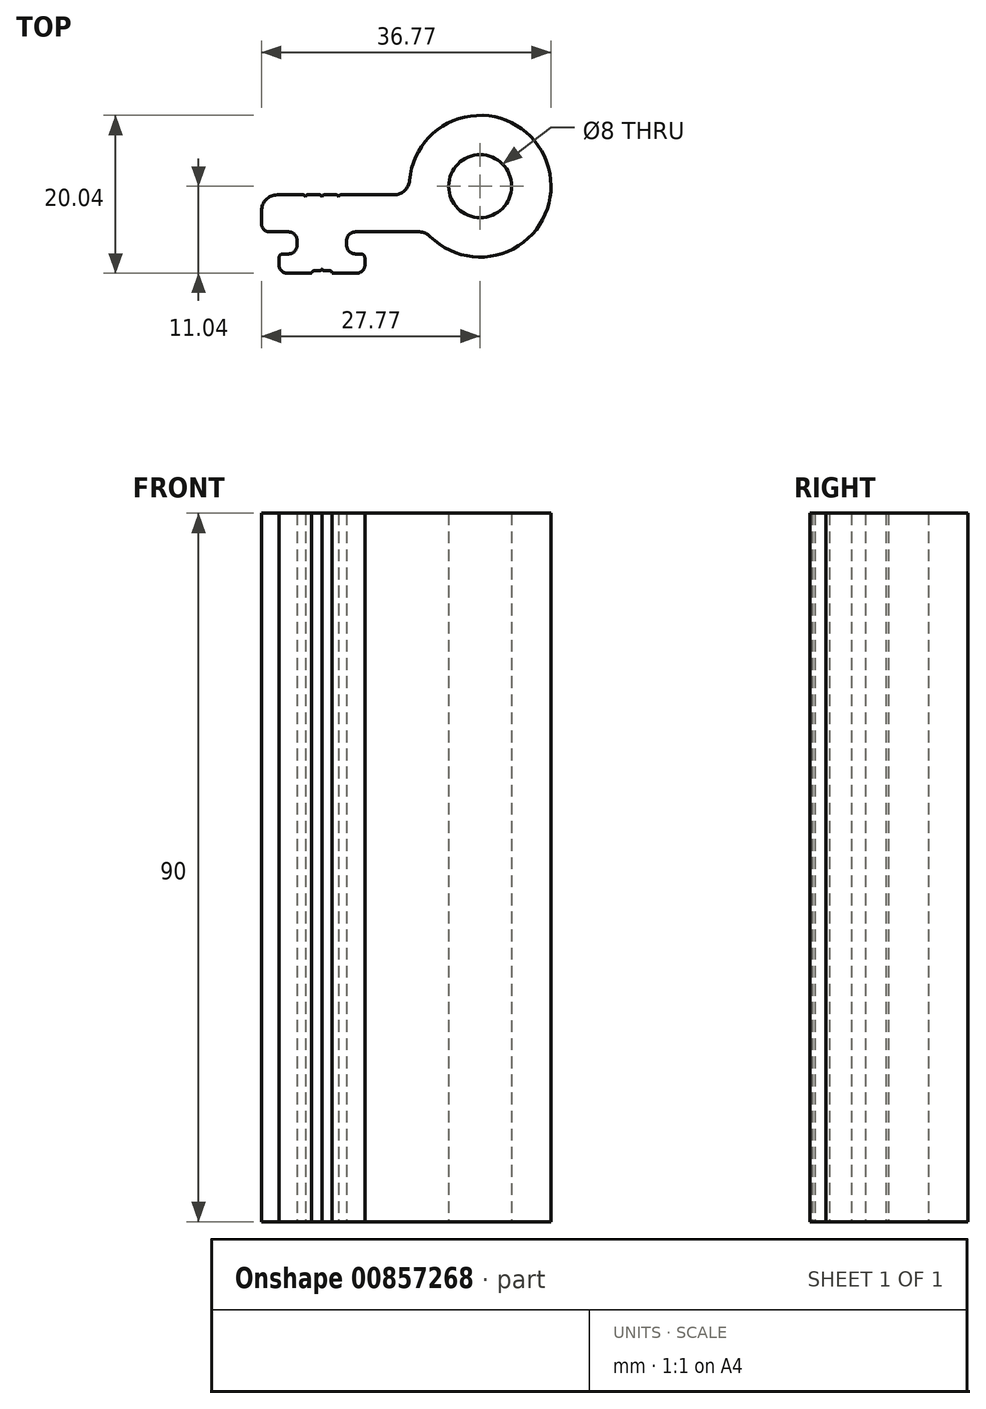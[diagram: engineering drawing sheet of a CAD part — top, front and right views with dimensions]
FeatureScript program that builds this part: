
annotation { "Feature Type Name" : "Feature", "Feature Type Description" : "" }
export const myFeature = defineFeature(function(context is Context, id is Id, definition is map)
    precondition{}
    {
        {
            var Q0;
            Q0=qCreatedBy(makeId("Top.planeOp"),FACE);
            var sketch = newSketch(context, id + "F0", { "sketchPlane" : qUnion([Q0])});
            skCircle(sketch, "E0", {"center": v(0, 0) * mm, "radius": 9 * mm});
            skCircle(sketch, "E1", {"center": v(0, 0) * mm, "radius": 4 * mm});
            skLineSegment(sketch, "E2", {"start": v(0, 0) * mm, "end": v(-45.8, 0) * mm, "construction": true});
            skLineSegment(sketch, "E3", {"start": v(-22.5, -1.1) * mm, "end": v(-25.77, -1.1) * mm});
            skLineSegment(sketch, "E4", {"start": v(-27.77, -3.1) * mm, "end": v(-27.77, -4.8) * mm});
            skLineSegment(sketch, "E5", {"start": v(-26.77, -5.8) * mm, "end": v(-24.35, -5.8) * mm});
            skPoint(sketch, "E6.visualSharp", {"position": v(-27.77, -1.1) * mm});
            skArc(sketch, "E6.filletArc", {"start": v(-25.77, -1.1) * mm, "mid": v(-27.18, -1.69) * mm, "end": v(-27.77, -3.1) * mm});
            skLineSegment(sketch, "E7", {"start": v(-23.25, -6.9) * mm, "end": v(-23.25, -7.5) * mm});
            skLineSegment(sketch, "E8", {"start": v(-24.35, -8.6) * mm, "end": v(-25.05, -8.6) * mm});
            skLineSegment(sketch, "E9", {"start": v(-25.55, -9.1) * mm, "end": v(-25.55, -10.04) * mm});
            skLineSegment(sketch, "E10", {"start": v(-24.55, -11.04) * mm, "end": v(-21.4, -11.04) * mm});
            skLineSegment(sketch, "E11", {"start": v(-14.65, -10.04) * mm, "end": v(-14.65, -9.1) * mm});
            skLineSegment(sketch, "E12", {"start": v(-15.15, -8.6) * mm, "end": v(-15.85, -8.6) * mm});
            skLineSegment(sketch, "E13", {"start": v(-16.95, -7.5) * mm, "end": v(-16.95, -6.9) * mm});
            skArc(sketch, "E14.filletArc", {"start": v(-15.65, -11.04) * mm, "mid": v(-14.94, -10.75) * mm, "end": v(-14.65, -10.04) * mm});
            skArc(sketch, "E15.filletArc", {"start": v(-25.55, -10.04) * mm, "mid": v(-25.26, -10.75) * mm, "end": v(-24.55, -11.04) * mm});
            skArc(sketch, "E16.filletArc", {"start": v(-22.2, -1.4) * mm, "mid": v(-22.29, -1.19) * mm, "end": v(-22.5, -1.1) * mm});
            skLineSegment(sketch, "E17", {"start": v(-21.72, -1.1) * mm, "end": v(-20.4, -1.1) * mm});
            skLineSegment(sketch, "E18", {"start": v(-17.7, -1.1) * mm, "end": v(-8.93, -1.1) * mm});
            skArc(sketch, "E19.filletArc", {"start": v(-18, -1.4) * mm, "mid": v(-18.09, -1.19) * mm, "end": v(-18.3, -1.1) * mm});
            skArc(sketch, "E20.filletArc", {"start": v(-17.7, -1.1) * mm, "mid": v(-17.91, -1.19) * mm, "end": v(-18, -1.4) * mm});
            skLineSegment(sketch, "E21", {"start": v(-19.8, -1.1) * mm, "end": v(-18.3, -1.1) * mm});
            skLineSegment(sketch, "E22", {"start": v(-21.4, -11.01) * mm, "end": v(-21.4, -11.04) * mm});
            skLineSegment(sketch, "E23", {"start": v(-19.8, -10.74) * mm, "end": v(-19.1, -10.74) * mm});
            skLineSegment(sketch, "E24", {"start": v(-18.8, -11.04) * mm, "end": v(-18.8, -11.04) * mm});
            skArc(sketch, "E25.filletArc", {"start": v(-21.1, -10.74) * mm, "mid": v(-21.31, -10.83) * mm, "end": v(-21.4, -11.04) * mm});
            skArc(sketch, "E26.filletArc", {"start": v(-18.8, -11.04) * mm, "mid": v(-18.89, -10.83) * mm, "end": v(-19.1, -10.74) * mm});
            skArc(sketch, "E27.filletArc", {"start": v(-20.1, -1.4) * mm, "mid": v(-20.19, -1.19) * mm, "end": v(-20.4, -1.1) * mm});
            skLineSegment(sketch, "E28.trimOffspring", {"start": v(-18.8, -11.04) * mm, "end": v(-15.65, -11.04) * mm});
            skArc(sketch, "E29.filletArc", {"start": v(-27.77, -4.8) * mm, "mid": v(-27.48, -5.5) * mm, "end": v(-26.77, -5.8) * mm});
            skArc(sketch, "E30.filletArc", {"start": v(-23.25, -6.9) * mm, "mid": v(-23.57, -6.12) * mm, "end": v(-24.35, -5.8) * mm});
            skArc(sketch, "E31.filletArc", {"start": v(-24.35, -8.6) * mm, "mid": v(-23.57, -8.28) * mm, "end": v(-23.25, -7.5) * mm});
            skArc(sketch, "E32.filletArc", {"start": v(-25.05, -8.6) * mm, "mid": v(-25.4, -8.75) * mm, "end": v(-25.55, -9.1) * mm});
            skLineSegment(sketch, "E33", {"start": v(-15.85, -5.8) * mm, "end": v(-6.88, -5.8) * mm});
            skArc(sketch, "E34.filletArc", {"start": v(-15.85, -5.8) * mm, "mid": v(-16.63, -6.12) * mm, "end": v(-16.95, -6.9) * mm});
            skArc(sketch, "E35.filletArc", {"start": v(-16.95, -7.5) * mm, "mid": v(-16.63, -8.28) * mm, "end": v(-15.85, -8.6) * mm});
            skArc(sketch, "E36.filletArc", {"start": v(-14.65, -9.1) * mm, "mid": v(-14.8, -8.75) * mm, "end": v(-15.15, -8.6) * mm});
            skArc(sketch, "E37.filletArc", {"start": v(-19.8, -1.1) * mm, "mid": v(-20.01, -1.19) * mm, "end": v(-20.1, -1.4) * mm});
            skLineSegment(sketch, "E38", {"start": v(-21.72, -1.1) * mm, "end": v(-21.9, -1.1) * mm});
            skArc(sketch, "E39.filletArc", {"start": v(-21.9, -1.1) * mm, "mid": v(-22.11, -1.19) * mm, "end": v(-22.2, -1.4) * mm});
            skLineSegment(sketch, "E40", {"start": v(9, 0) * mm, "end": v(9, -14.88) * mm, "construction": true});
            skLineSegment(sketch, "E41", {"start": v(-20.1, -0.66) * mm, "end": v(-20.1, -10.44) * mm, "construction": true});
            skLineSegment(sketch, "E42", {"start": v(-21.1, -10.74) * mm, "end": v(-20.4, -10.74) * mm});
            skArc(sketch, "E43.filletArc", {"start": v(-20.4, -10.74) * mm, "mid": v(-20.19, -10.66) * mm, "end": v(-20.1, -10.44) * mm});
            skArc(sketch, "E44.filletArc", {"start": v(-20.1, -10.44) * mm, "mid": v(-20.01, -10.66) * mm, "end": v(-19.8, -10.74) * mm});
            skSolve(sketch);
        }
        {
            var Q0;
            Q0=qSketchRegion(id+"F0",true);
            extrude(context, id + "F1", {"entities" : qUnion([Q0]), "endBound" : BoundingType.SYMMETRIC, "depth" : 90 * mm, "offsetDistance" : 25 * mm});
        }
        {
            var Q0;
            Q0=makeQuery(id+"F1.opExtrude","SWEPT_EDGE",EDGE,{"disambiguationData":[OSD([sQuery(id+"F0.wireOp",EDGE,"E0"),sQuery(id+"F0.wireOp",EDGE,"E3")])]});
            fillet(context, id + "F2", {"entities" : qUnion([Q0]), "radius" : 2 * mm, "tangentPropagation" : true, "allowEdgeOverflow" : false});
        }
    });
